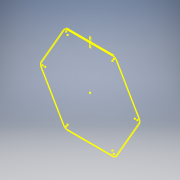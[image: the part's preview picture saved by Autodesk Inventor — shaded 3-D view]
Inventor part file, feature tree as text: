
AUTODESK INVENTOR PART (.ipt)
format: ipt  version: 2019 (Build 230136000, 136)  size: 189,952 bytes
history: native  units: mm
features: reference x6, projected_geometry x6, sketch x4, extrude x3, other x3
ambient origin geometry x8: Origin, YZ Plane, XZ Plane, XY Plane, X Axis, Y Axis, Z Axis, Center Point
bodies: Solid1 (feature_tree)
feature tree (22):
  extrude  "Extrusion1"  Depth=10.0mm
  sketch  "Sketch2"  dims[d2=4.0mm d3=0.0mm d4=3.0mm]
  extrude  "Extrusion2"  Depth=3.0mm
  extrude  "Extrusion3"  Depth=15.0mm TaperAngle=0.0deg
  sketch  "Sketch1"  dims[d0=10.0mm d1=10.0mm]
  reference  "Reference1"
  reference  "Reference2"
  reference  "Reference3"
  reference  "Reference4"
  reference  "Reference5"
  reference  "Reference6"
  projected_geometry  "Projected Loop1"
  sketch  "Sketch3"  dims[d5=3.0mm d6=15.0mm d7=0.0mm]
  sketch  "Sketch4"  dims[d8=3.0mm d9=3.0mm d10=3.0mm d11=3.0mm d12=3.0mm d13=0.0mm]
  projected_geometry  "Projected Loop2"
  projected_geometry  "Projected Loop3"
  projected_geometry  "Projected Loop4"
  projected_geometry  "Projected Loop5"
  projected_geometry  "Projected Loop6"
  other  "Assembly1"
  other  "Base v6 - 175:2"
  other  "Base v6 - 175:1"
